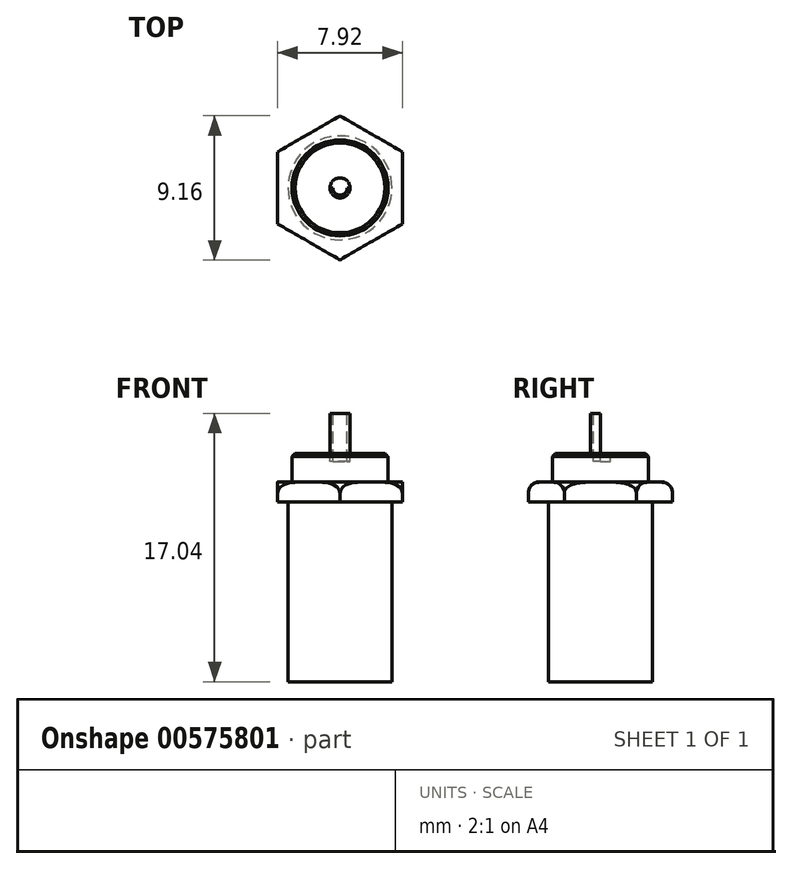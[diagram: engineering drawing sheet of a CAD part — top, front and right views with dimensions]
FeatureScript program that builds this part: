
annotation { "Feature Type Name" : "Feature", "Feature Type Description" : "" }
export const myFeature = defineFeature(function(context is Context, id is Id, definition is map)
    precondition{}
    {
        {
            var Q0;
            Q0=qCreatedBy(makeId("Front.planeOp"),FACE);
            var sketch = newSketch(context, id + "F0", { "sketchPlane" : qUnion([Q0])});
            skLineSegment(sketch, "E0", {"start": v(0, -20.37) * mm, "end": v(0, 18.13) * mm, "construction": true});
            skSolve(sketch);
        }
        {
            var Q0;
            Q0=qCreatedBy(makeId("Top.planeOp"),FACE);
            var sketch = newSketch(context, id + "F1", { "sketchPlane" : qUnion([Q0])});
            skCircle(sketch, "E1", {"center": v(0, 0) * mm, "radius": 3.96 * mm, "construction": true});
            skLineSegment(sketch, "E2.0", {"start": v(3.96, 2.29) * mm, "end": v(3.96, -2.29) * mm, "construction": true});
            skLineSegment(sketch, "E2.1", {"start": v(3.96, -2.29) * mm, "end": v(0, -4.58) * mm, "construction": true});
            skLineSegment(sketch, "E2.2", {"start": v(0, -4.58) * mm, "end": v(-3.96, -2.29) * mm, "construction": true});
            skLineSegment(sketch, "E2.3", {"start": v(-3.96, -2.29) * mm, "end": v(-3.96, 2.29) * mm, "construction": true});
            skLineSegment(sketch, "E2.4", {"start": v(-3.96, 2.29) * mm, "end": v(0, 4.58) * mm, "construction": true});
            skLineSegment(sketch, "E2.5", {"start": v(0, 4.58) * mm, "end": v(3.96, 2.29) * mm, "construction": true});
            skPoint(sketch, "E2.0.midPoint", {"position": v(3.96, 0) * mm});
            skLineSegment(sketch, "E3", {"start": v(0, 4.58) * mm, "end": v(3.96, 2.29) * mm});
            skLineSegment(sketch, "E4", {"start": v(3.96, 2.29) * mm, "end": v(3.96, -2.29) * mm});
            skLineSegment(sketch, "E5", {"start": v(3.96, -2.29) * mm, "end": v(0, -4.58) * mm});
            skLineSegment(sketch, "E6", {"start": v(0, -4.58) * mm, "end": v(-3.96, -2.29) * mm});
            skLineSegment(sketch, "E7", {"start": v(-3.96, -2.29) * mm, "end": v(-3.96, 2.29) * mm});
            skLineSegment(sketch, "E8", {"start": v(-3.96, 2.29) * mm, "end": v(0, 4.58) * mm});
            skSolve(sketch);
        }
        {
            var Q0;
            Q0 = qSketchRegion(id + "F1", true);
            extrude(context, id + "F2", {"entities" : qUnion([Q0]), "depth" : 1.27 * mm, "offsetDistance" : 25.4 * mm});
        }
        {
            var Q0;
            Q0=qCreatedBy(makeId("Right.planeOp"),FACE);
            var sketch = newSketch(context, id + "F3", { "sketchPlane" : qUnion([Q0])});
            skArc(sketch, "E9", {"start": v(4.58, 0.57) * mm, "mid": v(4.37, 1.06) * mm, "end": v(3.88, 1.27) * mm});
            skLineSegment(sketch, "E10", {"start": v(4.58, 0.57) * mm, "end": v(3.88, 0.57) * mm, "construction": true});
            skLineSegment(sketch, "E11", {"start": v(3.88, 1.27) * mm, "end": v(3.88, 0.57) * mm, "construction": true});
            skLineSegment(sketch, "E12", {"start": v(3.88, 1.27) * mm, "end": v(3.88, 1.27) * mm});
            skLineSegment(sketch, "E13", {"start": v(3.88, 1.27) * mm, "end": v(4.58, 1.27) * mm});
            skLineSegment(sketch, "E14", {"start": v(4.58, 1.27) * mm, "end": v(4.58, 0.57) * mm});
            skLineSegment(sketch, "E15", {"start": v(4.58, 0.57) * mm, "end": v(4.58, 0.57) * mm});
            skSolve(sketch);
        }
        {
            var Q0;
            Q0=makeQuery(id+"F3.imprint","IMPRINT",FACE,{"disambiguationData":[TD([[makeQuery(id+"F3.imprint","IMPRINT",EDGE,{"derivedFrom":sQuery(id+"F3.wireOp",EDGE,"E9")}),-1.0]])]});
            var Q1;
            Q1=sQuery(id+"F0.wireOp",EDGE,"E0");
            revolve(context, id + "F4", {"operationType" : NewBodyOperationType.REMOVE, "entities" : qUnion([Q0]), "axis" : qUnion([Q1]), "revolveType" : RevolveType.FULL, "oppositeDirection" : true});
        }
        {
            var Q0;
            Q0=makeQuery(id+"F2.opExtrude","CAP_FACE",FACE,{"disambiguationData":[OSD([sQuery(id+"F1.wireOp",EDGE,"E3"),sQuery(id+"F1.wireOp",EDGE,"E4"),sQuery(id+"F1.wireOp",EDGE,"E5"),sQuery(id+"F1.wireOp",EDGE,"E6"),sQuery(id+"F1.wireOp",EDGE,"E7"),sQuery(id+"F1.wireOp",EDGE,"E8")])],"isStart":false});
            var sketch = newSketch(context, id + "F5", { "sketchPlane" : qUnion([Q0])});
            skCircle(sketch, "E16", {"center": v(0, 0) * mm, "radius": 3.05 * mm});
            skSolve(sketch);
        }
        {
            var Q0;
            Q0=makeQuery(id+"F5.imprint","IMPRINT",FACE,{"disambiguationData":[TD([[makeQuery(id+"F5.imprint","IMPRINT",EDGE,{"derivedFrom":sQuery(id+"F5.wireOp",EDGE,"E16")}),1.0]])]});
            extrude(context, id + "F6", {"entities" : qUnion([Q0]), "operationType" : NewBodyOperationType.ADD, "depth" : 1.8 * mm, "offsetDistance" : 25.4 * mm});
        }
        {
            var Q0;
            Q0=makeQuery(id+"F6.opExtrude","CAP_EDGE",EDGE,{"disambiguationData":[OSD([sQuery(id+"F5.wireOp",EDGE,"E16")])],"isStart":false});
            chamfer(context, id + "F7", {"entities" : qUnion([Q0]), "width" : 0.2 * mm, "tangentPropagation" : true});
        }
        {
            var Q0;
            Q0=makeQuery(id+"F6.opExtrude","CAP_FACE",FACE,{"disambiguationData":[OSD([sQuery(id+"F5.wireOp",EDGE,"E16")])],"isStart":false});
            var sketch = newSketch(context, id + "F8", { "sketchPlane" : qUnion([Q0])});
            skCircle(sketch, "E17", {"center": v(0, 0) * mm, "radius": 0.64 * mm});
            skSolve(sketch);
        }
        {
            var Q0;
            Q0=makeQuery(id+"F8.imprint","IMPRINT",FACE,{"disambiguationData":[TD([[makeQuery(id+"F8.imprint","IMPRINT",EDGE,{"derivedFrom":sQuery(id+"F8.wireOp",EDGE,"E17")}),1.0]])]});
            extrude(context, id + "F9", {"entities" : qUnion([Q0]), "operationType" : NewBodyOperationType.ADD, "depth" : 2.54 * mm, "offsetDistance" : 25.4 * mm});
        }
        {
            var Q0;
            Q0=makeQuery(id+"F9.opExtrude","CAP_FACE",FACE,{"disambiguationData":[OSD([sQuery(id+"F8.wireOp",EDGE,"E17")])],"isStart":false});
            var sketch = newSketch(context, id + "F10", { "sketchPlane" : qUnion([Q0])});
            skCircle(sketch, "E18", {"center": v(0, 0) * mm, "radius": 0.46 * mm, "construction": true});
            skLineSegment(sketch, "E19", {"start": v(-0.46, 0) * mm, "end": v(-0.64, 0) * mm});
            skArc(sketch, "E20", {"start": v(0.64, 0) * mm, "mid": v(0, 0.64) * mm, "end": v(-0.64, 0) * mm});
            skLineSegment(sketch, "E21", {"start": v(0.46, 0) * mm, "end": v(0.64, 0) * mm});
            skArc(sketch, "E22", {"start": v(0.46, 0) * mm, "mid": v(0, -0.46) * mm, "end": v(-0.46, 0) * mm});
            skSolve(sketch);
        }
        {
            var Q0;
            Q0=makeQuery(id+"F10.imprint","IMPRINT",FACE,{"disambiguationData":[TD([[makeQuery(id+"F10.imprint","IMPRINT",EDGE,{"derivedFrom":sQuery(id+"F10.wireOp",EDGE,"E19")}),-1.0]])]});
            extrude(context, id + "F11", {"entities" : qUnion([Q0]), "operationType" : NewBodyOperationType.REMOVE, "oppositeDirection" : true, "depth" : 3.05 * mm, "offsetDistance" : 25.4 * mm});
        }
        {
            var Q0;
            Q0=makeQuery(id+"F2.opExtrude","CAP_FACE",FACE,{"disambiguationData":[OSD([sQuery(id+"F1.wireOp",EDGE,"E3"),sQuery(id+"F1.wireOp",EDGE,"E4"),sQuery(id+"F1.wireOp",EDGE,"E5"),sQuery(id+"F1.wireOp",EDGE,"E6"),sQuery(id+"F1.wireOp",EDGE,"E7"),sQuery(id+"F1.wireOp",EDGE,"E8")])],"isStart":true});
            var sketch = newSketch(context, id + "F12", { "sketchPlane" : qUnion([Q0])});
            skCircle(sketch, "E23", {"center": v(0, 0) * mm, "radius": 3.3 * mm});
            skSolve(sketch);
        }
        {
            var Q0;
            Q0=makeQuery(id+"F12.imprint","IMPRINT",FACE,{"disambiguationData":[TD([[makeQuery(id+"F12.imprint","IMPRINT",EDGE,{"derivedFrom":sQuery(id+"F12.wireOp",EDGE,"E23")}),1.0]])]});
            extrude(context, id + "F13", {"entities" : qUnion([Q0]), "operationType" : NewBodyOperationType.ADD, "depth" : 11.43 * mm, "offsetDistance" : 25.4 * mm});
        }
    });
